# Revit family: 0044886 Lighting Fixture_Sylvania_DeltaWing-LED-Electronic_Ceiling Surface
name_source: partatom
category: Lighting Fixtures
revit_build: Autodesk Revit 2017 (Build: 20190507_1515(x64)
units: mm (PartAtom-declared; Revit-internal decimal feet)

## family parameters
Cut with Voids When Loaded = No
Host = Face
Light Source = Yes
OmniClass Number = 23.80.70.11.17
OmniClass Title = Specialized Lighting by Location or Use
Part Type = Normal
Room Calculation Point = No
Round Connector Dimension = Use Diameter
Shared = No

## types (1)
- DELTAWING LED69 DALI 3K 1200
    Apparent Load = 71 VA
    Assembly Code = D5020200
    Body Material = Steel_Sylvania_DeltaWing_White
    CRI (Ra) = > 80
    Cap Material = Plastic_Sylvania_DeltaWing_White
    Catalog Number = 0044886 DELTAWING LED69 DALI 3K 1200
    Color Filter = 16777215
    Default Elevation = 0 mm  [stored 0 ft]
    Description = Low profile surface and suspended LED diffuser luminaire DeltaWing LED is perfect to fulfil a wide range of applications, including educational environments, medical buildings, storage facilities and circulation areas including stairwells High performance: delivers up to 7,260lm (luminaire lumen output on 4,000K version), and up to 102lm/W (total system efficiency) Available in neutral white (4,000K) and warm white (3,000K) Smooth Polycarbonate extruded diffuser provides high efficiency, while minimising glare Precision prisms designed to optimise light output and reduce glare Options of non-dimmable, DALI, 3 hour maintained Emergency and Integrated Microwave sensor as standard Integrated Microwave sensor mounted discretely behind the diffuser helps further reduce energy and maintenance bills Suitable for suspended mounting using wire suspension kit (to be ordered seperately) BESA box connection possibility standard on product Long lifetime: 50,000 hours life at 70% of the original output L70 Energy class: A++, A+, A
    Diffuser Material = Polycarbonate_Sylvania_DeltaWing_Opal_3000K
    Dimming Lamp Color Temperature Shift = <None>
    Drive Current = 250mA
    Electrical Protection = Class I
    Emit from Line Length = 1160 mm
    Glare Control = UGR<23
    Glow Wire Test = 850 °C
    Height = 85 mm  [stored 0.278871 ft]
    IK Rating = IK08
    IP Rating = IP44
    Inrush Current (max. quantity per 16A C breaker) = 20
    LOR = 100%
    Lamp = Integrated LED
    Length = 1218 mm  [stored 3.99606 ft]
    Life = 50 000h
    Manufacturer = Feilo Sylvania
    Model = DELTAWING LED69 DALI 3K 1200
    Photometric Web File = 0044886_DELTAWINGLED69DALI3K1200-198122.ies
    Product Family = DELTAWING LED - ELECTRONIC
    Product Page URL = http://www.sylvania-lighting.com
    Ta Rating = -10°C  to +25°C
    Tilt Angle = -90.00°
    URL = http://www.sylvania-lighting.com
    Voltage = 230 V
    Voltage Comments = UNV (Universal Voltage; 220-240 Volt)
    Weight = 3.40 kg
    Width = 200 mm  [stored 0.656168 ft]

note: [stored X ft] marks values corroborated as IEEE doubles in the binary element streams (Revit-internal decimal feet)

## geometry (parser evidence)
native form markers: Blend x4, Sweep x4
no freeform markers — native parametric forms only
